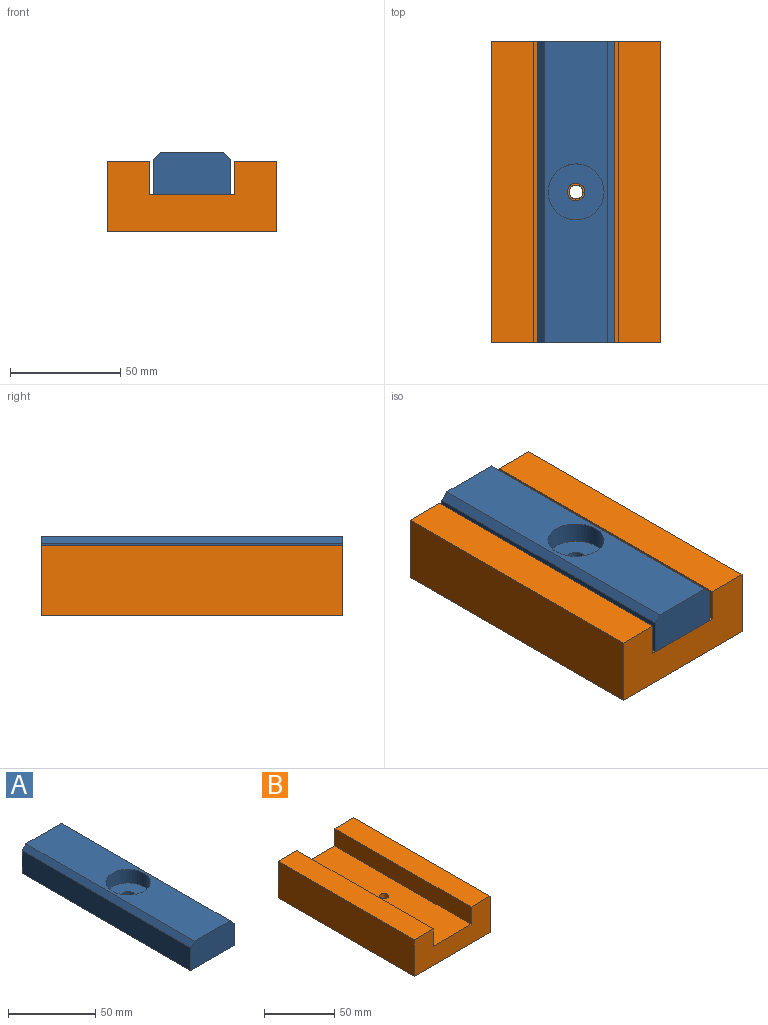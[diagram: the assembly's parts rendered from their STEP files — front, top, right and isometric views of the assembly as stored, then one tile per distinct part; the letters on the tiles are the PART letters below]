
ASSEMBLY  parts=2 mates=1
PART A: 11 faces, bbox 34.9x136.5x19.1 mm
  f0: cylinder r=3.97mm len=9.53mm, axis (0,0,-1), area 237.5mm2, adj f6,f9
  f1: plane 136.53x15.88mm, normal (-1,0,0), area 2167.3mm2, adj f2,f4,f6,f7
  f2: plane 34.93x19.05mm, normal (0,-1,0), area 655.2mm2, adj f1,f3,f5,f6,f7,f8
  f3: plane 136.53x15.88mm, normal (1,0,0), area 2167.3mm2, adj f2,f4,f6,f8
  f4: plane 34.93x19.05mm, normal (0,1,0), area 655.2mm2, adj f1,f3,f5,f6,f7,f8
  f5: plane 136.53x28.58mm, normal (0,0,1), area 3394.5mm2, adj f2,f4,f7,f8,f10
  f6: plane 136.53x34.93mm, normal (0,0,-1), area 4718.7mm2, adj f0,f1,f2,f3,f4
  f7: plane 136.53x3.18mm, normal (-0.71,0,0.71), area 613mm2, adj f1,f2,f4,f5
  f8: plane 136.53x3.18mm, normal (0.71,0,0.71), area 613mm2, adj f2,f3,f4,f5
  f9: plane 25.4x25.4mm, normal (0,0,1), area 457.2mm2, adj f0,f10
  f10: cylinder r=12.7mm len=25.4mm, axis (0,0,1), area 760.1mm2, adj f5,f9
PART B: 13 faces, bbox 76.2x136.5x31.8 mm
  f0: plane 136.53x19.05mm, normal (0,0,1), area 2600.8mm2, adj f1,f7,f8,f9
  f1: plane 136.53x15.06mm, normal (-1,0,0), area 2056.2mm2, adj f0,f2,f8,f9
  f2: plane 136.53x38.1mm, normal (0,0,1), area 5169.9mm2, adj f1,f3,f8,f9,f12
  f3: plane 136.53x15.06mm, normal (1,0,0), area 2056.2mm2, adj f2,f4,f8,f9
  f4: plane 136.53x19.05mm, normal (0,0,1), area 2600.8mm2, adj f3,f5,f8,f9
  f5: plane 136.53x31.75mm, normal (-1,0,0), area 4334.7mm2, adj f4,f6,f8,f9
  f6: plane 136.53x76.2mm, normal (0,0,-1), area 10118.2mm2, adj f5,f7,f8,f9,f10
  f7: plane 136.53x31.75mm, normal (1,0,0), area 4334.7mm2, adj f0,f6,f8,f9
  f8: plane 76.2x31.75mm, normal (0,-1,0), area 1845.5mm2, adj f0,f1,f2,f3,f4,f5,f6,f7
  f9: plane 76.2x31.75mm, normal (0,1,0), area 1845.5mm2, adj f0,f1,f2,f3,f4,f5,f6,f7
  f10: cylinder r=9.53mm len=19.05mm, axis (0,0,-1), area 760.1mm2, adj f6,f11
  f11: plane 19.05x19.05mm, normal (0,0,-1), area 253.4mm2, adj f10,f12
  f12: cylinder r=3.17mm len=6.35mm, axis (0,0,1), area 79.6mm2, adj f2,f11
PLACE A t=(-10.07,-106.92,-25.55)mm
PLACE B at identity
MATE fastened A.f0 <-> B.f10  axis (0,0,-1) through (-10.07,-68.26,-25.55)mm
